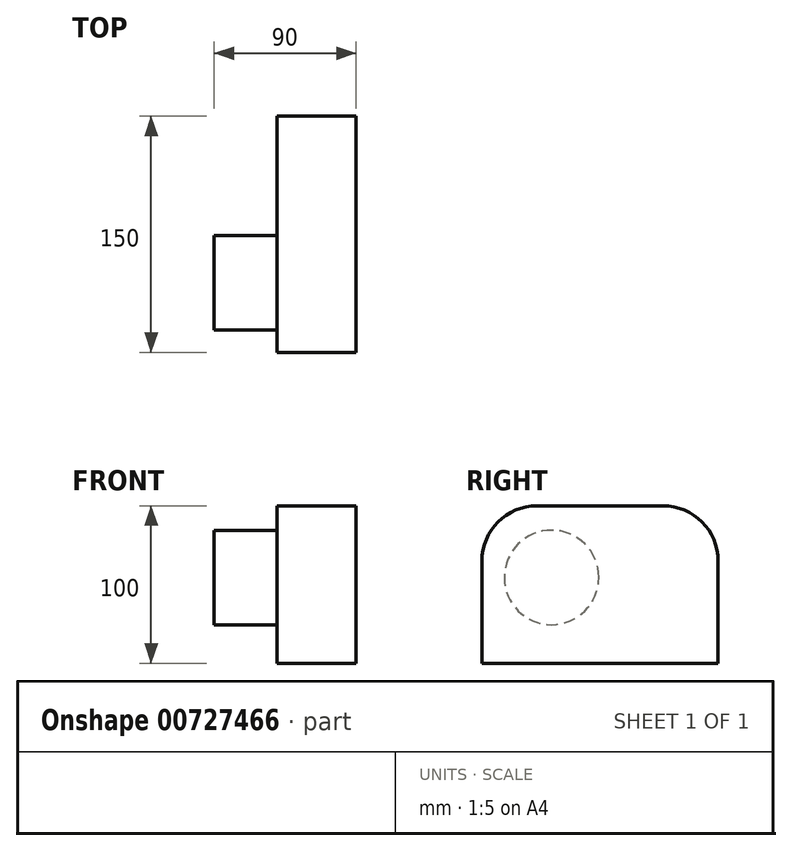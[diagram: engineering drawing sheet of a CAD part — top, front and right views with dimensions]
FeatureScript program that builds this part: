
annotation { "Feature Type Name" : "Feature", "Feature Type Description" : "" }
export const myFeature = defineFeature(function(context is Context, id is Id, definition is map)
    precondition{}
    {
        {
            var Q0;
            Q0=qCreatedBy(makeId("Top.planeOp"),FACE);
            var sketch = newSketch(context, id + "F0", { "sketchPlane" : qUnion([Q0])});
            skLineSegment(sketch, "E0.bottom", {"start": v(-176.1, 118.27) * mm, "end": v(-126.1, 118.27) * mm});
            skLineSegment(sketch, "E0.top", {"start": v(-176.1, -31.73) * mm, "end": v(-126.1, -31.73) * mm});
            skLineSegment(sketch, "E0.left", {"start": v(-176.1, 118.27) * mm, "end": v(-176.1, -31.73) * mm});
            skLineSegment(sketch, "E0.right", {"start": v(-126.1, 118.27) * mm, "end": v(-126.1, -31.73) * mm});
            skSolve(sketch);
        }
        {
            var Q0;
            Q0=makeQuery(id+"F0.imprint","IMPRINT",FACE,{"disambiguationData":[TD([[makeQuery(id+"F0.imprint","IMPRINT",EDGE,{"derivedFrom":sQuery(id+"F0.wireOp",EDGE,"E0.bottom")}),-1.0]])]});
            extrude(context, id + "F1", {"entities" : qUnion([Q0]), "depth" : 100 * mm, "offsetDistance" : 25 * mm});
        }
        {
            var Q0;
            Q0=makeQuery(id+"F1.opExtrude","SWEPT_FACE",FACE,{"disambiguationData":[OSD([sQuery(id+"F0.wireOp",EDGE,"E0.left")])]});
            var sketch = newSketch(context, id + "F2", { "sketchPlane" : qUnion([Q0])});
            skCircle(sketch, "E1", {"center": v(-12.5, 54.52) * mm, "radius": 30 * mm});
            skSolve(sketch);
        }
        {
            var Q0;
            Q0=makeQuery(id+"F2.imprint","IMPRINT",FACE,{"disambiguationData":[TD([[makeQuery(id+"F2.imprint","IMPRINT",EDGE,{"derivedFrom":sQuery(id+"F2.wireOp",EDGE,"E1")}),1.0]])]});
            extrude(context, id + "F3", {"entities" : qUnion([Q0]), "operationType" : NewBodyOperationType.ADD, "depth" : 40 * mm, "offsetDistance" : 25 * mm});
        }
        {
            var Q0;
            Q0=makeQuery(id+"F1.opExtrude","CAP_EDGE",EDGE,{"disambiguationData":[OSD([sQuery(id+"F0.wireOp",EDGE,"E0.bottom")])],"isStart":false});
            fillet(context, id + "F4", {"entities" : qUnion([Q0]), "radius" : 35 * mm, "tangentPropagation" : true, "allowEdgeOverflow" : false});
        }
        {
            var Q0;
            Q0=makeQuery(id+"F1.opExtrude","CAP_EDGE",EDGE,{"disambiguationData":[OSD([sQuery(id+"F0.wireOp",EDGE,"E0.top")])],"isStart":false});
            fillet(context, id + "F5", {"entities" : qUnion([Q0]), "radius" : 35 * mm, "tangentPropagation" : true, "allowEdgeOverflow" : false});
        }
    });
